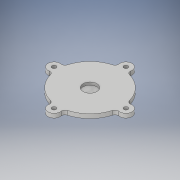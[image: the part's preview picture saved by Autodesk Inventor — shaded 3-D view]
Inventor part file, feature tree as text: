
AUTODESK INVENTOR PART (.ipt)
format: ipt  version: 2019 (Build 230136000, 136)  size: 553,472 bytes
history: native  units: in
note: dims shown in document units (in); Inventor stores cm internally (conversion verified against a paired STEP export)
features: extrude x5, sketch x5, fillet x1
ambient origin geometry x8: Origin, YZ Plane, XZ Plane, XY Plane, X Axis, Y Axis, Z Axis, Center Point
bodies: Solid1 (feature_tree)
feature tree (11):
  extrude  "Extrusion1"  Depth=0.15in TaperAngle=0.0deg
  extrude  "Extrusion2"  Depth=0.15in
  extrude  "Extrusion3"  Depth=0.125in
  extrude  "Extrusion4"  Depth=0.15in
  fillet  "Fillet1"  Radius=0.15in
  extrude  "Extrusion5"  Depth=0.15in TaperAngle=0.0deg
  sketch  "Sketch1"  dims[d0=0.15in d1=0.0in d2=0.15in d3=0.0in]
  sketch  "Sketch2"  dims[d4=0.15in d5=0.0in d6=0.5in]
  sketch  "Sketch3"  dims[d7=0.1in d8=0.0in d9=0.125in]
  sketch  "Sketch4"  dims[d10=0.15in d11=0.15in d12=0.15in]
  sketch  "Sketch5"  dims[d13=0.15in d14=0.2in d15=0.0in]
